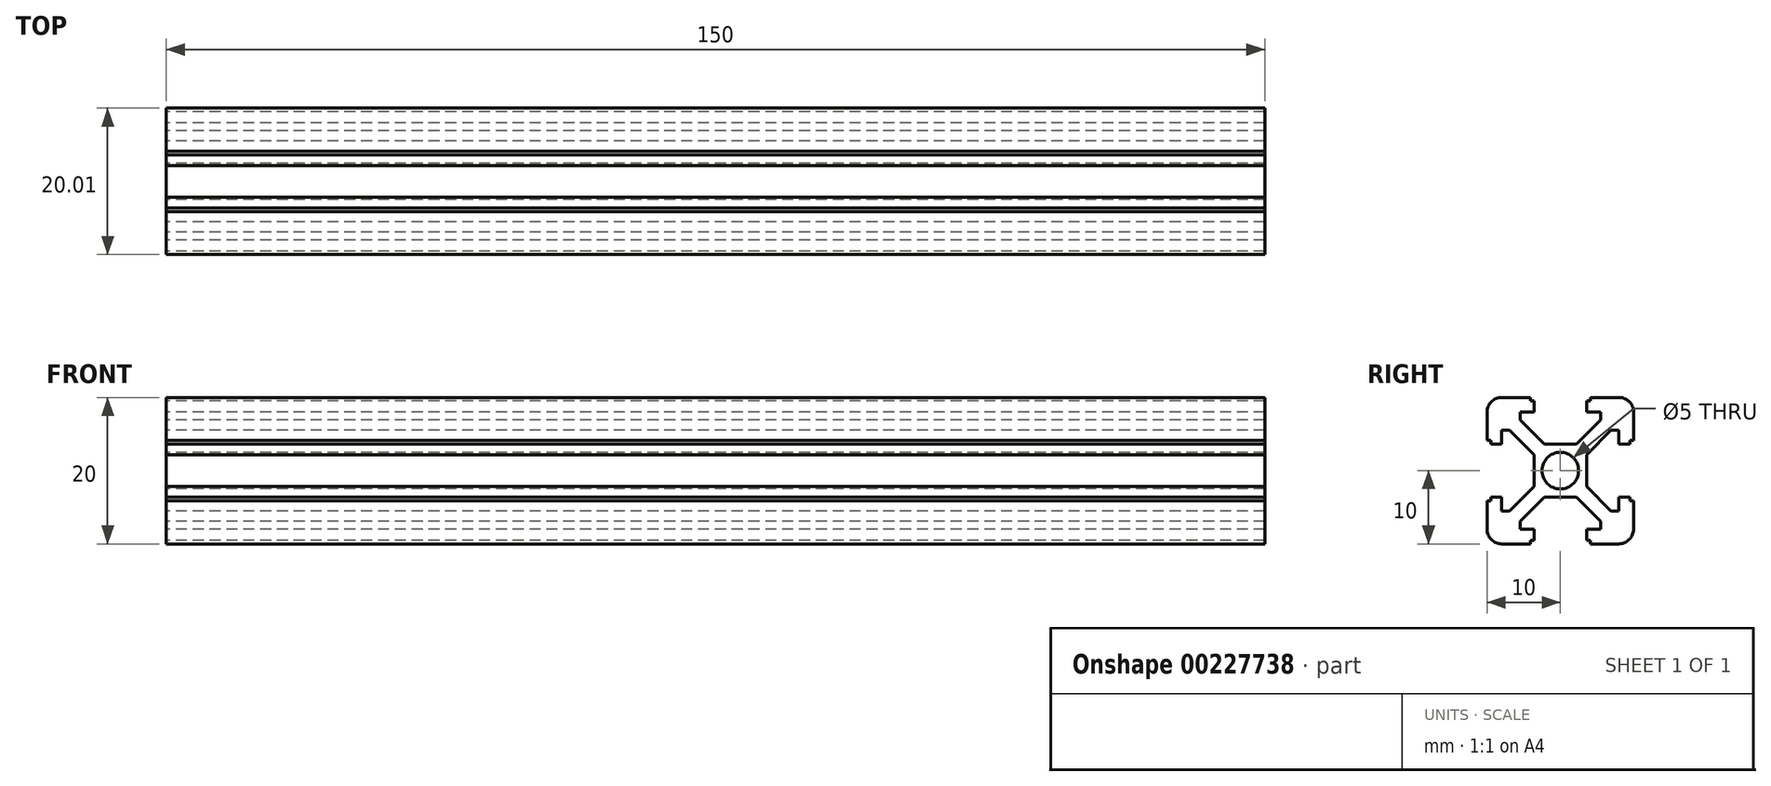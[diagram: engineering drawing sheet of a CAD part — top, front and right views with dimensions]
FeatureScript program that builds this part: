
annotation { "Feature Type Name" : "Feature", "Feature Type Description" : "" }
export const myFeature = defineFeature(function(context is Context, id is Id, definition is map)
    precondition{}
    {
        {
            var Q0;
            Q0=qCreatedBy(makeId("Right.planeOp"),FACE);
            var sketch = newSketch(context, id + "F0", { "sketchPlane" : qUnion([Q0])});
            skLineSegment(sketch, "E0", {"start": v(8, 10) * mm, "end": v(4.1, 10) * mm});
            skLineSegment(sketch, "E1", {"start": v(-10, 8) * mm, "end": v(-10, 4.1) * mm});
            skLineSegment(sketch, "E2", {"start": v(-8, -10) * mm, "end": v(-4.1, -10) * mm});
            skLineSegment(sketch, "E3", {"start": v(10, -8) * mm, "end": v(10, -4.1) * mm});
            skLineSegment(sketch, "E4", {"start": v(10, 10) * mm, "end": v(10, 9.97) * mm});
            skCircle(sketch, "E5", {"center": v(0, 0) * mm, "radius": 2.5 * mm});
            skLineSegment(sketch, "E6", {"start": v(-3.6, 0) * mm, "end": v(-3.6, 2.19) * mm});
            skLineSegment(sketch, "E7", {"start": v(0, 3.6) * mm, "end": v(-2.19, 3.6) * mm});
            skLineSegment(sketch, "E8", {"start": v(-9.5, 3.6) * mm, "end": v(-8, 3.6) * mm});
            skLineSegment(sketch, "E9", {"start": v(3.6, 0) * mm, "end": v(3.6, 2.19) * mm});
            skLineSegment(sketch, "E10", {"start": v(3.6, 9.5) * mm, "end": v(3.6, 8) * mm});
            skLineSegment(sketch, "E11", {"start": v(0, -3.6) * mm, "end": v(2.19, -3.6) * mm});
            skLineSegment(sketch, "E12", {"start": v(9.5, -3.6) * mm, "end": v(8, -3.6) * mm});
            skLineSegment(sketch, "E13", {"start": v(-3.6, 0) * mm, "end": v(-3.6, -2.19) * mm});
            skLineSegment(sketch, "E14.0", {"start": v(-6.91, 5.5) * mm, "end": v(-3.6, 2.19) * mm});
            skLineSegment(sketch, "E15.0", {"start": v(10.02, 9.98) * mm, "end": v(10, 9.97) * mm});
            skLineSegment(sketch, "E16.0", {"start": v(5.5, 6.91) * mm, "end": v(2.19, 3.6) * mm});
            skPoint(sketch, "E17.startSnap0", {"position": v(0, 10) * mm});
            skLineSegment(sketch, "E18", {"start": v(5.5, 8) * mm, "end": v(5.5, 6.91) * mm});
            skLineSegment(sketch, "E19", {"start": v(8, -5.5) * mm, "end": v(6.91, -5.5) * mm});
            skLineSegment(sketch, "E20", {"start": v(8, 5.5) * mm, "end": v(6.91, 5.5) * mm});
            skLineSegment(sketch, "E21", {"start": v(-5.5, 8) * mm, "end": v(-5.5, 6.91) * mm});
            skLineSegment(sketch, "E22.trimOffspring", {"start": v(-4.1, 10) * mm, "end": v(-8, 10) * mm});
            skLineSegment(sketch, "E23.trimOffspring", {"start": v(-3.6, 8) * mm, "end": v(-5.5, 8) * mm});
            skLineSegment(sketch, "E24.trimOffspring", {"start": v(3.6, 8) * mm, "end": v(3.6, 9.5) * mm});
            skLineSegment(sketch, "E25.trimOffspring", {"start": v(-3.6, 8) * mm, "end": v(-3.6, 9.5) * mm});
            skPoint(sketch, "E17.start.orphan", {"position": v(0, 13.55) * mm});
            skLineSegment(sketch, "E26.trimOffspring", {"start": v(-10, -4.1) * mm, "end": v(-10, -8) * mm});
            skLineSegment(sketch, "E27.trimOffspring", {"start": v(-8, -3.6) * mm, "end": v(-8, -5.5) * mm});
            skLineSegment(sketch, "E28.trimOffspring", {"start": v(-2.19, 3.6) * mm, "end": v(2.19, 3.6) * mm});
            skLineSegment(sketch, "E29.trimOffspring", {"start": v(-8, 3.6) * mm, "end": v(-9.5, 3.6) * mm});
            skLineSegment(sketch, "E30.trimOffspring", {"start": v(-8, -3.6) * mm, "end": v(-9.5, -3.6) * mm});
            skLineSegment(sketch, "E31.trimOffspring", {"start": v(4.1, -10) * mm, "end": v(8, -10) * mm});
            skLineSegment(sketch, "E32.trimOffspring", {"start": v(3.6, -8) * mm, "end": v(5.5, -8) * mm});
            skLineSegment(sketch, "E33.trimOffspring", {"start": v(-3.6, -8) * mm, "end": v(-3.6, -9.5) * mm});
            skLineSegment(sketch, "E34.trimOffspring", {"start": v(3.6, -8) * mm, "end": v(3.6, -9.5) * mm});
            skLineSegment(sketch, "E35.trimOffspring", {"start": v(8, 3.6) * mm, "end": v(9.5, 3.6) * mm});
            skLineSegment(sketch, "E36.trimOffspring", {"start": v(2.19, -3.6) * mm, "end": v(-2.19, -3.6) * mm});
            skLineSegment(sketch, "E37.trimOffspring", {"start": v(8, -3.6) * mm, "end": v(9.5, -3.6) * mm});
            skLineSegment(sketch, "E38.trimOffspring", {"start": v(6.91, 5.5) * mm, "end": v(3.6, 2.19) * mm});
            skLineSegment(sketch, "E39.trimOffspring", {"start": v(5.5, 8) * mm, "end": v(3.6, 8) * mm});
            skLineSegment(sketch, "E40.trimOffspring", {"start": v(8, 5.5) * mm, "end": v(8, 3.6) * mm});
            skLineSegment(sketch, "E41.trimOffspring", {"start": v(10, 5.5) * mm, "end": v(10, 4.1) * mm});
            skLineSegment(sketch, "E42", {"start": v(10, 8) * mm, "end": v(10, 5.5) * mm});
            skLineSegment(sketch, "E43.trimOffspring", {"start": v(3.6, 2.19) * mm, "end": v(3.6, -2.19) * mm});
            skLineSegment(sketch, "E44.trimOffspring", {"start": v(3.6, -2.19) * mm, "end": v(6.91, -5.5) * mm});
            skLineSegment(sketch, "E45.trimOffspring", {"start": v(-2.19, -3.6) * mm, "end": v(-5.5, -6.91) * mm});
            skLineSegment(sketch, "E46.trimOffspring", {"start": v(2.19, -3.6) * mm, "end": v(5.5, -6.91) * mm});
            skLineSegment(sketch, "E47.trimOffspring", {"start": v(-3.6, -2.19) * mm, "end": v(-6.91, -5.5) * mm});
            skLineSegment(sketch, "E48.trimOffspring", {"start": v(0, 0) * mm, "end": v(0.02, -0.02) * mm});
            skLineSegment(sketch, "E49.trimOffspring", {"start": v(-8, 5.5) * mm, "end": v(-8, 3.6) * mm});
            skLineSegment(sketch, "E50.trimOffspring", {"start": v(-5.5, 6.91) * mm, "end": v(-2.19, 3.6) * mm});
            skLineSegment(sketch, "E51.trimOffspring", {"start": v(-6.91, 5.5) * mm, "end": v(-8, 5.5) * mm});
            skLineSegment(sketch, "E52.trimOffspring", {"start": v(-6.91, -5.5) * mm, "end": v(-8, -5.5) * mm});
            skLineSegment(sketch, "E53.trimOffspring", {"start": v(-5.5, -6.91) * mm, "end": v(-5.5, -8) * mm});
            skLineSegment(sketch, "E54.trimOffspring", {"start": v(-9.97, -10) * mm, "end": v(-9.98, -10.02) * mm});
            skLineSegment(sketch, "E55.trimOffspring", {"start": v(-5.5, -8) * mm, "end": v(-3.6, -8) * mm});
            skLineSegment(sketch, "E56.trimOffspring", {"start": v(5.5, -6.91) * mm, "end": v(5.5, -8) * mm});
            skLineSegment(sketch, "E57.trimOffspring", {"start": v(8, -5.5) * mm, "end": v(8, -3.6) * mm});
            skPoint(sketch, "E58.visualSharp", {"position": v(-10, 10) * mm});
            skArc(sketch, "E58.filletArc", {"start": v(-8, 10) * mm, "mid": v(-9.41, 9.41) * mm, "end": v(-10, 8) * mm});
            skPoint(sketch, "E59.newPointA", {"position": v(10, 10) * mm});
            skArc(sketch, "E59.filletArc", {"start": v(10, 8) * mm, "mid": v(9.43, 9.41) * mm, "end": v(8, 10) * mm});
            skPoint(sketch, "E60.visualSharp", {"position": v(10, -10) * mm});
            skArc(sketch, "E60.filletArc", {"start": v(8, -10) * mm, "mid": v(9.41, -9.41) * mm, "end": v(10, -8) * mm});
            skPoint(sketch, "E61.visualSharp", {"position": v(-10, -10) * mm});
            skArc(sketch, "E61.filletArc", {"start": v(-10, -8) * mm, "mid": v(-9.41, -9.41) * mm, "end": v(-8, -10) * mm});
            skLineSegment(sketch, "E62", {"start": v(-9.5, 3.6) * mm, "end": v(-9.5, 4.1) * mm});
            skLineSegment(sketch, "E63", {"start": v(-9.5, 4.1) * mm, "end": v(-10, 4.1) * mm});
            skLineSegment(sketch, "E64", {"start": v(-9.5, -3.6) * mm, "end": v(-9.5, -4.1) * mm});
            skLineSegment(sketch, "E65", {"start": v(-9.5, -4.1) * mm, "end": v(-10, -4.1) * mm});
            skLineSegment(sketch, "E66", {"start": v(-3.6, -9.5) * mm, "end": v(-4.1, -9.5) * mm});
            skLineSegment(sketch, "E67", {"start": v(-4.1, -9.5) * mm, "end": v(-4.1, -10) * mm});
            skLineSegment(sketch, "E68", {"start": v(4.1, -10) * mm, "end": v(4.1, -9.5) * mm});
            skLineSegment(sketch, "E69", {"start": v(4.1, -9.5) * mm, "end": v(3.6, -9.5) * mm});
            skLineSegment(sketch, "E70", {"start": v(9.5, -3.6) * mm, "end": v(9.5, -4.1) * mm});
            skLineSegment(sketch, "E71", {"start": v(9.5, -4.1) * mm, "end": v(10, -4.1) * mm});
            skLineSegment(sketch, "E72", {"start": v(9.5, 3.6) * mm, "end": v(9.5, 4.1) * mm});
            skLineSegment(sketch, "E73", {"start": v(9.5, 4.1) * mm, "end": v(10, 4.1) * mm});
            skPoint(sketch, "E74.orphan", {"position": v(-10, -3.6) * mm});
            skPoint(sketch, "E75.start.orphan", {"position": v(10, 3.6) * mm});
            skPoint(sketch, "E76.start.orphan", {"position": v(3.6, -10) * mm});
            skPoint(sketch, "E77.orphan", {"position": v(-3.6, -10) * mm});
            skLineSegment(sketch, "E78", {"start": v(-3.6, 9.5) * mm, "end": v(-4.1, 9.5) * mm});
            skLineSegment(sketch, "E79", {"start": v(-4.1, 9.5) * mm, "end": v(-4.1, 10) * mm});
            skLineSegment(sketch, "E80", {"start": v(3.6, 9.5) * mm, "end": v(4.1, 9.5) * mm});
            skLineSegment(sketch, "E81", {"start": v(4.1, 9.5) * mm, "end": v(4.1, 10) * mm});
            skPoint(sketch, "E82.start.orphan", {"position": v(3.6, 10) * mm});
            skPoint(sketch, "E83.start.orphan", {"position": v(-3.6, 10) * mm});
            skSolve(sketch);
        }
        {
            var Q0;
            Q0 = qSketchRegion(id + "F0", true);
            extrude(context, id + "F1", {"entities" : qUnion([Q0]), "depth" : 150 * mm});
        }
    });
